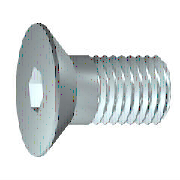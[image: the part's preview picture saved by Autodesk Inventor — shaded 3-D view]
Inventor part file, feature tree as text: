
AUTODESK INVENTOR PART (.ipt)
format: ipt  version: 2020 (Build 240168000, 168)  size: 178,176 bytes
history: native  units: mm (DEFAULTED — no unit token found)
features: sketch x2, extrude x1, plane x1
ambient origin geometry x7: Origin, YZ Plane, XY Plane, X Axis, Y Axis, Z Axis, Center Point
bodies: Solid1 (feature_tree), Body (feature_tree)
feature tree (4):
  sketch  "Sketch2"  dims[d2=1.5mm d3=4.0mm d6=2.48mm d7=45.0deg d8=2.886751mm d9=60.0deg d10=7.53mm d11=4.0mm d12=0.429415mm d13=90.0deg d30=10.0mm d14=0.0mm d15=20.0mm d16=0.0mm d17=0.429415mm d18=0.429415mm d20=0.0mm d39=45.0deg d43=0.0mm d44=0.0mm]
  extrude  "Slot"  Depth=20.0mm
  plane  "Work Plane1"
  sketch  "Sketch1"  dims[d0=30.0mm d1=20.0mm]
